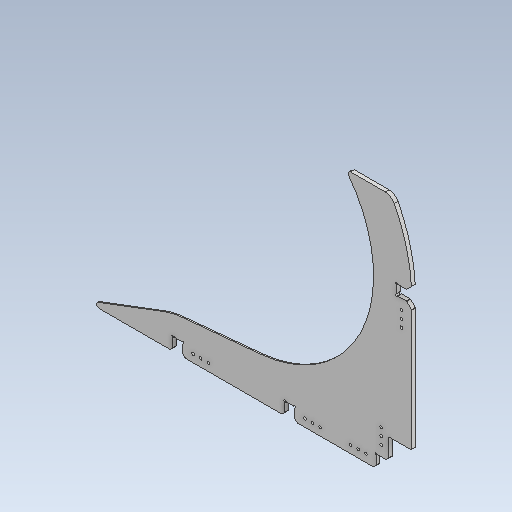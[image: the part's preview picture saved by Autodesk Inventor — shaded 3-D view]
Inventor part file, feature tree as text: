
AUTODESK INVENTOR PART (.ipt)
format: ipt  version: 2020 (Build 240168000, 168)  size: 258,048 bytes
history: native  units: in
note: dims shown in document units (in); Inventor stores cm internally (conversion verified against a paired STEP export)
features: sketch x4, other x3
ambient origin geometry x8: Origin, YZ Plane, XZ Plane, XY Plane, X Axis, Y Axis, Z Axis, Center Point
bodies: Solid1 (feature_tree)
feature tree (7):
  other  "Ball_IndexerC.ipt"
  other  "Solid1::Ball_IndexerC.ipt"
  other  "TaggingFeature1"
  sketch  "Sketch1"  dims[d0=0.3937in]
  sketch  "Sketch2"
  sketch  "Sketch3"
  sketch  "Sketch4"
